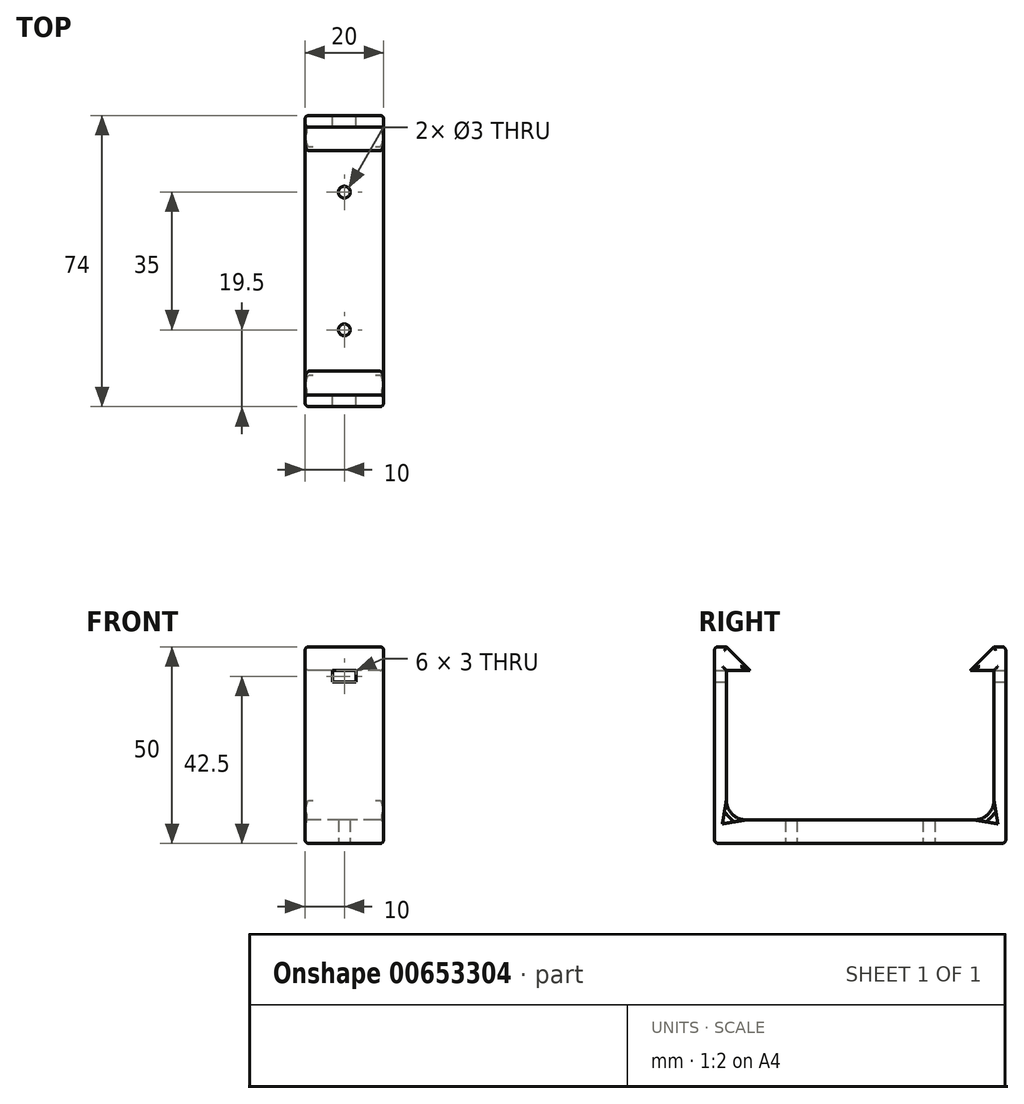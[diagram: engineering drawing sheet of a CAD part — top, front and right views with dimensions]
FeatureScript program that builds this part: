
annotation { "Feature Type Name" : "Feature", "Feature Type Description" : "" }
export const myFeature = defineFeature(function(context is Context, id is Id, definition is map)
    precondition{}
    {
        {
            var Q0;
            Q0=qCreatedBy(makeId("Top.planeOp"),FACE);
            var sketch = newSketch(context, id + "F0", { "sketchPlane" : qUnion([Q0])});
            skLineSegment(sketch, "E0.bottom", {"start": v(10, 0) * mm, "end": v(-10, 0) * mm});
            skLineSegment(sketch, "E0.top", {"start": v(10, 37) * mm, "end": v(-10, 37) * mm});
            skLineSegment(sketch, "E0.left", {"start": v(10, 0) * mm, "end": v(10, 37) * mm});
            skLineSegment(sketch, "E0.right", {"start": v(-10, 0) * mm, "end": v(-10, 37) * mm});
            skPoint(sketch, "E0.middle", {"position": v(0, 0) * mm});
            skCircle(sketch, "E1", {"center": v(0, 17.5) * mm, "radius": 1.5 * mm});
            skSolve(sketch);
        }
        {
            var Q0;
            Q0 = qSketchRegion(id + "F0", true);
            extrude(context, id + "F1", {"entities" : qUnion([Q0]), "depth" : 50 * mm, "offsetDistance" : 25 * mm});
        }
        {
            var Q0;
            Q0=makeQuery(id+"F1.opExtrude","SWEPT_FACE",FACE,{"disambiguationData":[OSD([sQuery(id+"F0.wireOp",EDGE,"E0.right")])]});
            var sketch = newSketch(context, id + "F2", { "sketchPlane" : qUnion([Q0])});
            skLineSegment(sketch, "E2.top", {"start": v(0, 6) * mm, "end": v(-34, 6) * mm});
            skLineSegment(sketch, "E2.right", {"start": v(-34, 44) * mm, "end": v(-34, 6) * mm});
            skLineSegment(sketch, "E3", {"start": v(-34, 50) * mm, "end": v(-28, 44) * mm});
            skLineSegment(sketch, "E4", {"start": v(-28, 44) * mm, "end": v(-34, 44) * mm});
            skLineSegment(sketch, "E5", {"start": v(-34, 50) * mm, "end": v(0, 50) * mm});
            skLineSegment(sketch, "E6", {"start": v(0, 50) * mm, "end": v(0, 6) * mm});
            skSolve(sketch);
        }
        {
            var Q0;
            Q0 = qSketchRegion(id + "F2", true);
            extrude(context, id + "F3", {"entities" : qUnion([Q0]), "operationType" : NewBodyOperationType.REMOVE, "endBound" : BoundingType.THROUGH_ALL, "oppositeDirection" : true, "depth" : 25 * mm, "offsetDistance" : 25 * mm});
        }
        {
            var Q0;
            Q0=makeQuery(id+"F1.opExtrude","SWEPT_BODY",BODY,{"disambiguationData":[OSD([sQuery(id+"F0.wireOp",EDGE,"E0.bottom"),sQuery(id+"F0.wireOp",EDGE,"E0.top"),sQuery(id+"F0.wireOp",EDGE,"E0.left"),sQuery(id+"F0.wireOp",EDGE,"E0.right"),sQuery(id+"F0.wireOp",EDGE,"E1")])]});
            var Q1;
            Q1=qCreatedBy(makeId("Front.planeOp"),FACE);
            mirror(context, id + "F4", {"operationType" : NewBodyOperationType.ADD, "entities" : qUnion([Q0]), "mirrorPlane" : qUnion([Q1])});
        }
        {
            var Q0;
            {var subQ0=makeQuery(id+"F1.opExtrude","SWEPT_FACE",FACE,{"disambiguationData":[OSD([sQuery(id+"F0.wireOp",EDGE,"E0.right")])]});Q0=makeQuery(id+"F4.boolean.opBoolean","MERGE",FACE,{"derivedFrom":[subQ0,makeQuery(id+"F4.opPattern","COPY",FACE,{"derivedFrom":subQ0,"instanceName":"1"})]});}
            var Q1;
            Q1=makeQuery(id+"F1.opExtrude","SWEPT_FACE",FACE,{"disambiguationData":[OSD([sQuery(id+"F0.wireOp",EDGE,"E0.top")])]});
            var Q2;
            Q2=makeQuery(id+"F4.opPattern","COPY",FACE,{"derivedFrom":makeQuery(id+"F1.opExtrude","SWEPT_FACE",FACE,{"disambiguationData":[OSD([sQuery(id+"F0.wireOp",EDGE,"E0.top")])]}),"instanceName":"1"});
            var Q3;
            {var subQ0=makeQuery(id+"F1.opExtrude","SWEPT_FACE",FACE,{"disambiguationData":[OSD([sQuery(id+"F0.wireOp",EDGE,"E0.left")])]});Q3=makeQuery(id+"F4.boolean.opBoolean","MERGE",FACE,{"derivedFrom":[subQ0,makeQuery(id+"F4.opPattern","COPY",FACE,{"derivedFrom":subQ0,"instanceName":"1"})]});}
            fillet(context, id + "F5", {"entities" : qUnion([Q0, Q1, Q2, Q3]), "radius" : 1 * mm, "tangentPropagation" : true, "allowEdgeOverflow" : false});
        }
        {
            var Q0;
            Q0=makeQuery(id+"F3.boolean.opBoolean","COPY",EDGE,{"derivedFrom":makeQuery(id+"F3.opExtrude","SWEPT_EDGE",EDGE,{"disambiguationData":[OSD([sQuery(id+"F2.wireOp",EDGE,"E2.top"),sQuery(id+"F2.wireOp",EDGE,"E2.right")])]})});
            var Q1;
            Q1=makeQuery(id+"F4.opPattern","COPY",EDGE,{"derivedFrom":makeQuery(id+"F3.boolean.opBoolean","COPY",EDGE,{"derivedFrom":makeQuery(id+"F3.opExtrude","SWEPT_EDGE",EDGE,{"disambiguationData":[OSD([sQuery(id+"F2.wireOp",EDGE,"E2.top"),sQuery(id+"F2.wireOp",EDGE,"E2.right")])]})}),"instanceName":"1"});
            fillet(context, id + "F6", {"entities" : qUnion([Q0, Q1]), "radius" : 5 * mm, "tangentPropagation" : true, "allowEdgeOverflow" : false});
        }
        {
            var Q0;
            Q0=qCreatedBy(makeId("Front.planeOp"),FACE);
            var sketch = newSketch(context, id + "F7", { "sketchPlane" : qUnion([Q0])});
            skLineSegment(sketch, "E7.bottom", {"start": v(-3, 44) * mm, "end": v(3, 44) * mm});
            skLineSegment(sketch, "E7.top", {"start": v(-3, 41) * mm, "end": v(3, 41) * mm});
            skLineSegment(sketch, "E7.left", {"start": v(-3, 44) * mm, "end": v(-3, 41) * mm});
            skLineSegment(sketch, "E7.right", {"start": v(3, 44) * mm, "end": v(3, 41) * mm});
            skSolve(sketch);
        }
        {
            var Q0;
            Q0 = qSketchRegion(id + "F7", true);
            extrude(context, id + "F8", {"entities" : qUnion([Q0]), "operationType" : NewBodyOperationType.REMOVE, "endBound" : BoundingType.THROUGH_ALL, "depth" : 25 * mm, "offsetDistance" : 25 * mm, "hasSecondDirection" : true, "secondDirectionBound" : SecondDirectionBoundingType.THROUGH_ALL, "secondDirectionOppositeDirection" : true, "secondDirectionDepth" : 25 * mm});
        }
    });
